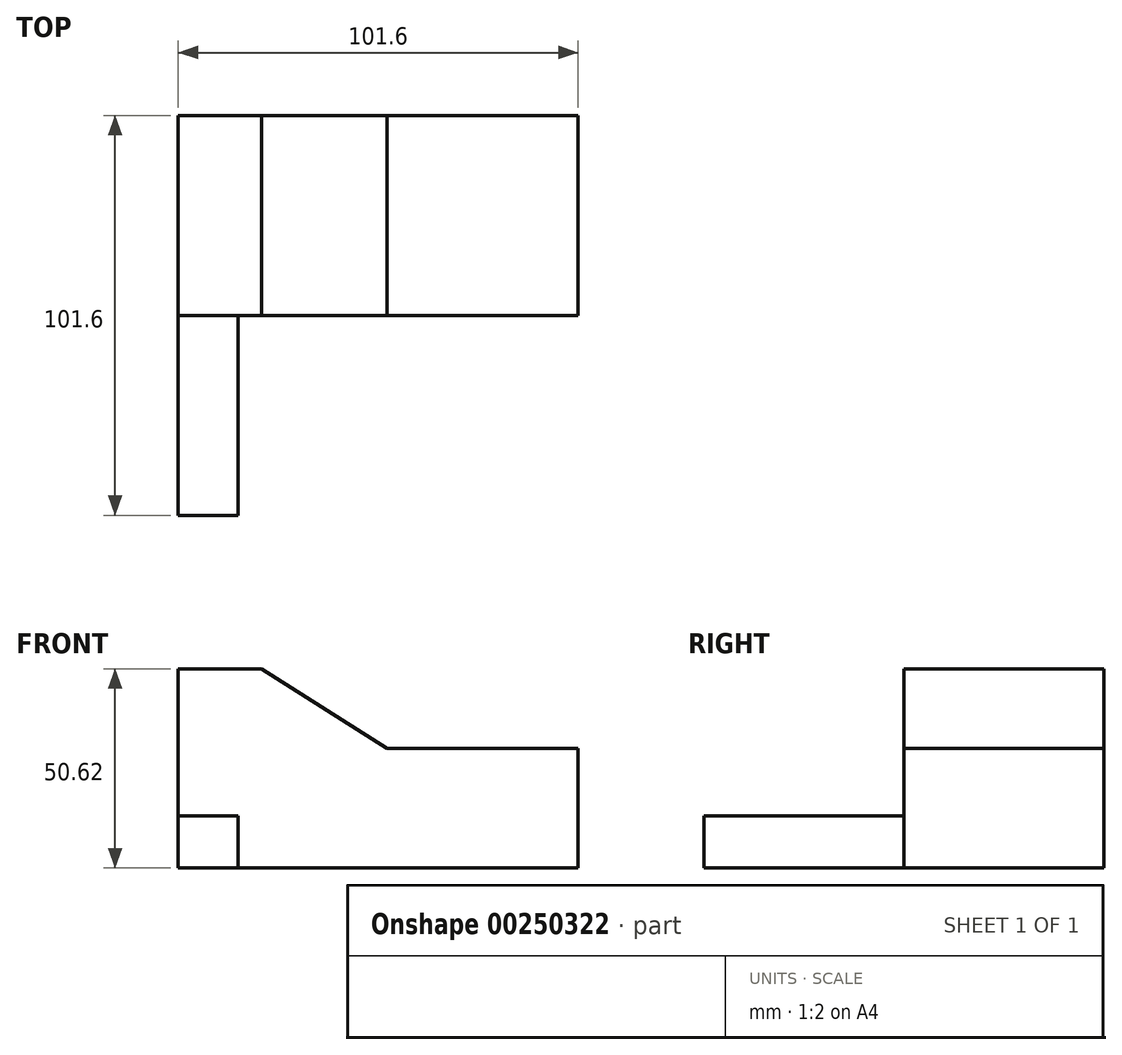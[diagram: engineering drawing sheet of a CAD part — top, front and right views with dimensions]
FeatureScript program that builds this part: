
annotation { "Feature Type Name" : "Feature", "Feature Type Description" : "" }
export const myFeature = defineFeature(function(context is Context, id is Id, definition is map)
    precondition{}
    {
        {
            var Q0;
            Q0=qCreatedBy(makeId("Front.planeOp"),FACE);
            var sketch = newSketch(context, id + "F0", { "sketchPlane" : qUnion([Q0])});
            skPoint(sketch, "E0.end.orphan", {"position": v(0, -9.71) * mm});
            skLineSegment(sketch, "E1", {"start": v(-71.15, -50.62) * mm, "end": v(30.45, -50.62) * mm});
            skLineSegment(sketch, "E2", {"start": v(-71.15, -50.62) * mm, "end": v(-71.15, 0) * mm});
            skPoint(sketch, "E3.start.orphan", {"position": v(32.7, -50.62) * mm});
            skLineSegment(sketch, "E4", {"start": v(30.45, -50.62) * mm, "end": v(30.45, -20.27) * mm});
            skLineSegment(sketch, "E5", {"start": v(30.45, -20.27) * mm, "end": v(-18.09, -20.27) * mm});
            skLineSegment(sketch, "E6", {"start": v(-71.15, 0) * mm, "end": v(-49.98, 0) * mm});
            skLineSegment(sketch, "E7", {"start": v(-49.98, 0) * mm, "end": v(-18.09, -20.27) * mm});
            skSolve(sketch);
        }
        {
            var Q0;
            Q0=makeQuery(id+"F0.imprint","IMPRINT",FACE,{"disambiguationData":[TD([[makeQuery(id+"F0.imprint","IMPRINT",EDGE,{"derivedFrom":sQuery(id+"F0.wireOp",EDGE,"E1")}),1.0]])]});
            extrude(context, id + "F1", {"entities" : qUnion([Q0]), "depth" : 50.8 * mm});
        }
        {
            var Q0;
            Q0=makeQuery(id+"F1.opExtrude","CAP_FACE",FACE,{"disambiguationData":[OSD([sQuery(id+"F0.wireOp",EDGE,"E1"),sQuery(id+"F0.wireOp",EDGE,"E2"),sQuery(id+"F0.wireOp",EDGE,"E4"),sQuery(id+"F0.wireOp",EDGE,"E5"),sQuery(id+"F0.wireOp",EDGE,"E6"),sQuery(id+"F0.wireOp",EDGE,"E7")])],"isStart":false});
            var sketch = newSketch(context, id + "F2", { "sketchPlane" : qUnion([Q0])});
            skLineSegment(sketch, "E8", {"start": v(-71.15, -37.3) * mm, "end": v(-55.9, -37.3) * mm});
            skLineSegment(sketch, "E9", {"start": v(-55.9, -37.3) * mm, "end": v(-55.9, -50.62) * mm});
            skSolve(sketch);
        }
        {
            var Q0;
            {var subQ0=sQuery(id+"F2.wireOp",EDGE,"E8");Q0=makeQuery(id+"F2.imprint","IMPRINT",FACE,{"disambiguationData":[TD([[makeQuery(id+"F2.imprint","IMPRINT",EDGE,{"derivedFrom":subQ0}),-1.0]])]});}
            extrude(context, id + "F3", {"entities" : qUnion([Q0]), "operationType" : NewBodyOperationType.ADD, "depth" : 50.8 * mm});
        }
    });
